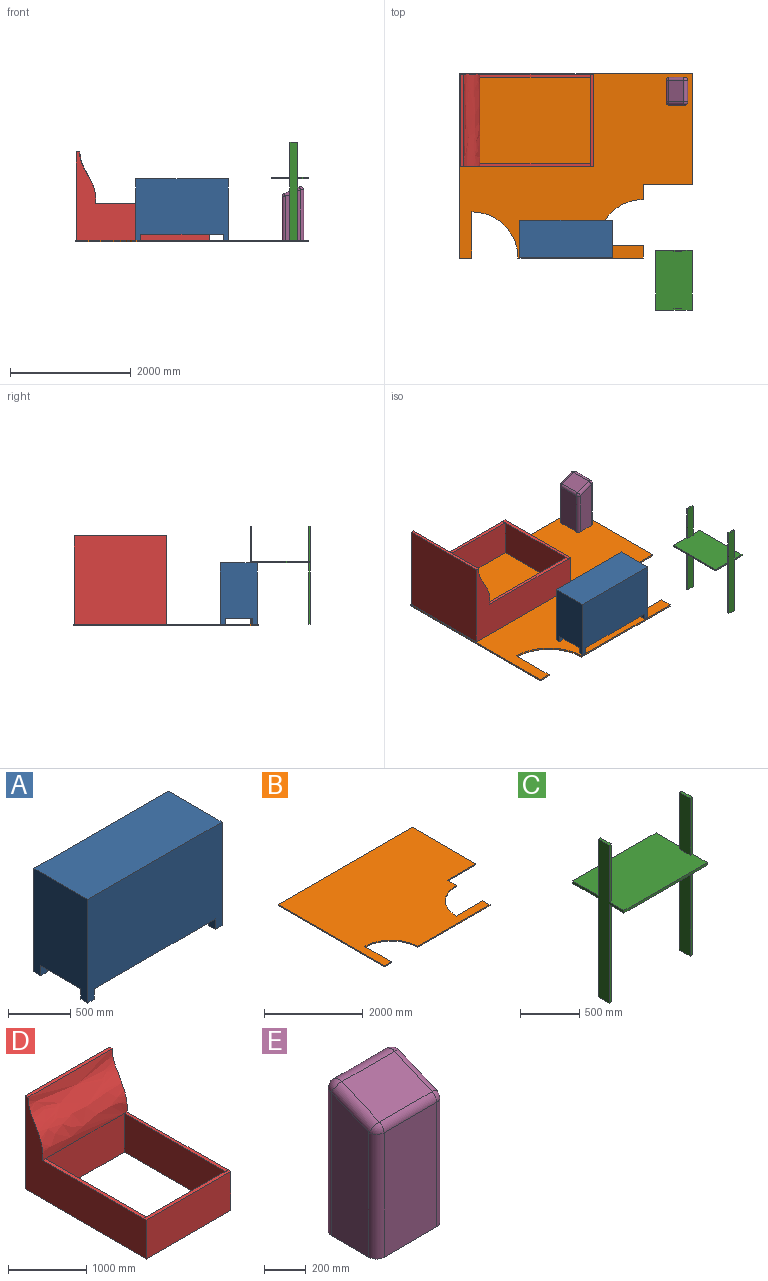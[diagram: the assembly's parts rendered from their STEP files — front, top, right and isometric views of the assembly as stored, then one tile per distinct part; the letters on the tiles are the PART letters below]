
ASSEMBLY  parts=5 mates=3
PART A: 18 faces, bbox 1524x609.6x1016 mm
  f0: plane 1016x609.6mm, normal (-1,0,0), area 572902.1mm2, adj f1,f3,f4,f5,f6,f8,f9,f11
  f1: plane 1524x1016mm, normal (0,-1,0), area 1409029.4mm2, adj f0,f2,f4,f5,f7,f8,f16,f17
  f2: plane 1016x609.6mm, normal (1,0,0), area 572902.1mm2, adj f1,f3,f4,f5,f12,f14,f15,f17
  f3: plane 1524x1016mm, normal (0,1,0), area 1409029.4mm2, adj f0,f2,f4,f5,f10,f11,f13,f14
  f4: plane 1524x609.6mm, normal (0,0,1), area 929030.4mm2, adj f0,f1,f2,f3
  f5: plane 1524x609.6mm, normal (0,0,-1), area 905804.6mm2, adj f0,f1,f2,f3,f6,f7,f9,f10
  f6: plane 101.6x76.2mm, normal (0,1,0), area 7741.9mm2, adj f0,f5,f7,f8
  f7: plane 101.6x76.2mm, normal (1,0,0), area 7741.9mm2, adj f1,f5,f6,f8
  f8: plane 76.2x76.2mm, normal (0,0,-1), area 5806.4mm2, adj f0,f1,f6,f7
  f9: plane 101.6x76.2mm, normal (0,-1,0), area 7741.9mm2, adj f0,f5,f10,f11
  f10: plane 101.6x76.2mm, normal (1,0,0), area 7741.9mm2, adj f3,f5,f9,f11
  f11: plane 76.2x76.2mm, normal (0,0,-1), area 5806.4mm2, adj f0,f3,f9,f10
  f12: plane 101.6x76.2mm, normal (0,-1,0), area 7741.9mm2, adj f2,f5,f13,f14
  f13: plane 101.6x76.2mm, normal (-1,0,0), area 7741.9mm2, adj f3,f5,f12,f14
  f14: plane 76.2x76.2mm, normal (0,0,-1), area 5806.4mm2, adj f2,f3,f12,f13
  f15: plane 101.6x76.2mm, normal (0,1,0), area 7741.9mm2, adj f2,f5,f16,f17
  f16: plane 101.6x76.2mm, normal (-1,0,0), area 7741.9mm2, adj f1,f5,f15,f17
  f17: plane 76.2x76.2mm, normal (0,0,-1), area 5806.4mm2, adj f1,f2,f15,f16
PART B: 14 faces, bbox 3848.1x3048x25.4 mm
  f0: plane 762x25.4mm, normal (0,1,0), area 19354.8mm2, adj f1,f11,f12,f13
  f1: cylinder r=762mm len=762mm, axis (0,0,1), area 30402.4mm2, adj f0,f2,f12,f13
  f2: plane 254x25.4mm, normal (1,0,0), area 6451.6mm2, adj f1,f3,f12,f13
  f3: plane 812.8x25.4mm, normal (0,-1,0), area 20645.1mm2, adj f2,f4,f12,f13
  f4: plane 1828.8x25.4mm, normal (1,0,0), area 46451.5mm2, adj f3,f5,f12,f13
  f5: plane 3848.1x25.4mm, normal (0,1,0), area 97741.7mm2, adj f4,f6,f12,f13
  f6: plane 3048x25.4mm, normal (-1,0,0), area 77419.2mm2, adj f5,f7,f12,f13
  f7: plane 203.2x25.4mm, normal (0,-1,0), area 5161.3mm2, adj f6,f8,f12,f13
  f8: plane 762x25.4mm, normal (1,0,0), area 19354.8mm2, adj f7,f9,f12,f13
  f9: cylinder r=762mm len=762mm, axis (0,0,1), area 30402.4mm2, adj f8,f10,f12,f13
  f10: plane 2070.1x25.4mm, normal (0,-1,0), area 52580.5mm2, adj f9,f11,f12,f13
  f11: plane 203.2x25.4mm, normal (1,0,0), area 5161.3mm2, adj f0,f10,f12,f13
  f12: plane 3848.1x3048mm, normal (0,0,-1), area 9825969.6mm2, adj f0,f1,f2,f3,f4,f5,f6,f7
  f13: plane 3848.1x3048mm, normal (0,0,1), area 9825969.6mm2, adj f0,f1,f2,f3,f4,f5,f6,f7
PART C: 22 faces, bbox 990.6x609.6x1625.6 mm
  f0: plane 990.6x609.6mm, normal (0,0,1), area 597418.2mm2, adj f2,f3,f4,f5,f10,f11,f12,f18
  f1: plane 990.6x609.6mm, normal (0,0,-1), area 597418.2mm2, adj f2,f3,f4,f5,f7,f8,f9,f15
  f2: plane 1625.6x609.6mm, normal (1,0,0), area 218709.2mm2, adj f0,f1,f3,f5,f14,f15,f17,f18
  f3: plane 990.6x25.4mm, normal (0,1,0), area 25161.2mm2, adj f0,f1,f2,f4
  f4: plane 1625.6x609.6mm, normal (-1,0,0), area 218709.2mm2, adj f0,f1,f3,f5,f6,f7,f9,f10
  f5: plane 990.6x25.4mm, normal (0,-1,0), area 25161.2mm2, adj f0,f1,f2,f4
  f6: plane 127x25.4mm, normal (0,0,-1), area 3225.8mm2, adj f4,f7,f8,f9
  f7: plane 1016x25.4mm, normal (0,-1,0), area 25806.4mm2, adj f1,f4,f6,f8
  f8: plane 1016x127mm, normal (1,0,0), area 129032mm2, adj f1,f6,f7,f9
  f9: plane 1016x25.4mm, normal (0,1,0), area 25806.4mm2, adj f1,f4,f6,f8
  f10: plane 584.2x25.4mm, normal (0,1,0), area 14838.7mm2, adj f0,f4,f11,f13
  f11: plane 584.2x127mm, normal (1,0,0), area 74193.4mm2, adj f0,f10,f12,f13
  f12: plane 584.2x25.4mm, normal (0,-1,0), area 14838.7mm2, adj f0,f4,f11,f13
  f13: plane 127x25.4mm, normal (0,0,1), area 3225.8mm2, adj f4,f10,f11,f12
  f14: plane 127x25.4mm, normal (0,0,-1), area 3225.8mm2, adj f2,f15,f16,f17
  f15: plane 1016x25.4mm, normal (0,1,0), area 25806.4mm2, adj f1,f2,f14,f16
  f16: plane 1016x127mm, normal (-1,0,0), area 129032mm2, adj f1,f14,f15,f17
  f17: plane 1016x25.4mm, normal (0,-1,0), area 25806.4mm2, adj f1,f2,f14,f16
  f18: plane 584.2x25.4mm, normal (0,-1,0), area 14838.7mm2, adj f0,f2,f19,f21
  f19: plane 584.2x127mm, normal (-1,0,0), area 74193.4mm2, adj f0,f18,f20,f21
  f20: plane 584.2x25.4mm, normal (0,1,0), area 14838.7mm2, adj f0,f2,f19,f21
  f21: plane 127x25.4mm, normal (0,0,1), area 3225.8mm2, adj f2,f18,f19,f20
PART D: 14 faces, bbox 1524x2198.3x1462.2 mm
  f0: plane 1422.4x606.76mm, normal (0,-1,0), area 863057.9mm2, adj f1,f4,f8,f9
  f1: plane 2198.35x1524mm, normal (0,0,-1), area 748998.7mm2, adj f0,f2,f5,f6,f8,f9,f11,f13
  f2: plane 1524x1462.24mm, normal (0,1,0), area 2228453.5mm2, adj f1,f3,f5,f6
  f3: plane 1524x50.8mm, normal (0,0,1), area 77419.2mm2, adj f2,f4,f5,f6
  f4: extruded ~1524x855.48mm, area 1390335.4mm2, adj f0,f3,f5,f6,f7,f10
  f5: plane 2198.35x1462.24mm, normal (-1,0,0), area 1505538.4mm2, adj f1,f2,f3,f4,f10,f11,f12,f13
  f6: plane 2198.35x1462.24mm, normal (1,0,0), area 1505538.4mm2, adj f1,f2,f3,f4,f7,f11,f12,f13
  f7: plane 1828.8x50.8mm, normal (0,0,1), area 92903mm2, adj f4,f6,f8,f11
  f8: plane 1828.8x606.76mm, normal (-1,0,0), area 1109645.9mm2, adj f0,f1,f7,f11
  f9: plane 1828.8x606.76mm, normal (1,0,0), area 1109645.9mm2, adj f0,f1,f10,f11
  f10: plane 1828.8x50.8mm, normal (0,0,1), area 92903mm2, adj f4,f5,f9,f11
  f11: plane 1524x609.6mm, normal (0,1,0), area 867383.4mm2, adj f1,f5,f6,f7,f8,f9,f10,f12
  f12: plane 1524x50.8mm, normal (0,0,1), area 77419.2mm2, adj f5,f6,f11,f13
  f13: plane 1524x609.6mm, normal (0,-1,0), area 929030.4mm2, adj f1,f5,f6,f12
PART E: 18 faces, bbox 457.2x355.6x888.2 mm
  f0: plane 728.5x355.6mm, normal (0,-1,0), area 259055.6mm2, adj f4,f8,f13,f14
  f1: plane 837.36x254mm, normal (1,0,0), area 198864.5mm2, adj f4,f6,f7,f8
  f2: plane 837.36x254mm, normal (-1,0,0), area 198864.5mm2, adj f4,f11,f14,f17
  f3: plane 837.36x355.6mm, normal (0,1,0), area 297765.2mm2, adj f4,f6,f11,f12
  f4: plane 457.2x355.6mm, normal (0,0,-1), area 160365.1mm2, adj f0,f1,f2,f3,f6,f8,f11,f14
  f5: plane 355.6x254mm, normal (0,-0.39,0.92), area 98267.8mm2, adj f7,f12,f13,f17
  f6: cylinder r=50.8mm len=837.36mm, axis (0,0,1), area 66818.3mm2, adj f1,f3,f4,f9
  f7: cylinder r=50.8mm len=274.01mm, axis (0,0.92,0.39), area 22051.3mm2, adj f1,f5,f9,f10
  f8: cylinder r=50.8mm len=728.5mm, axis (0,0,-1), area 58131.9mm2, adj f0,f1,f4,f10
  f9: sphere r=50.8mm, area 5098.5mm2, adj f6,f7,f12
  f10: sphere r=50.8mm, area 3008.8mm2, adj f7,f8,f13
  f11: cylinder r=50.8mm len=837.36mm, axis (0,0,-1), area 66818.3mm2, adj f2,f3,f4,f15
  f12: cylinder r=50.8mm len=355.6mm, axis (-1,0,0), area 35689.8mm2, adj f3,f5,f9,f15
  f13: cylinder r=50.8mm len=355.6mm, axis (1,0,0), area 21061.5mm2, adj f0,f5,f10,f16
  f14: cylinder r=50.8mm len=728.5mm, axis (0,0,1), area 58131.9mm2, adj f0,f2,f4,f16
  f15: sphere r=50.8mm, area 5098.5mm2, adj f11,f12,f17
  f16: sphere r=50.8mm, area 3008.8mm2, adj f13,f14,f17
  f17: cylinder r=50.8mm len=274.01mm, axis (0,0.92,0.39), area 22051.3mm2, adj f2,f5,f15,f16
PLACE A t=(-802.35,-1705.88,127)mm
PLACE B t=(-1799.28,-1718.23,25.4)mm fixed
PLACE C rot(axis=(0,0,1),90deg) t=(2048.82,-1593.03,1041.4)mm
PLACE D rot(axis=(0,0,1),90deg) t=(-907.77,1319.12,635)mm
PLACE E rot(axis=(0,0,-1),90deg) t=(1615.1,1265.97,25.4)mm
MATE planar B.f13 <-> D.f1  axis (0,0,1) through (0,0,25.4)mm
MATE planar A.f11 <-> B.f13  axis (0,0,-1) through (-764.25,-1134.38,25.4)mm
MATE planar E.f4 <-> B.f13  axis (0,0,-1) through (1792.9,1037.37,25.4)mm
